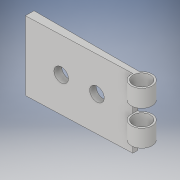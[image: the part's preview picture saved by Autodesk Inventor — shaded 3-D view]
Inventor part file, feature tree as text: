
AUTODESK INVENTOR PART (.ipt)
format: ipt  version: 2018 (Build 220112000, 112)  size: 144,896 bytes
history: native  units: in
note: dims shown in document units (in); Inventor stores cm internally (conversion verified against a paired STEP export)
features: extrude x4, sketch x4, plane x1
ambient origin geometry x8: Origin, YZ Plane, XZ Plane, XY Plane, X Axis, Y Axis, Z Axis, Center Point
bodies: Solid1 (feature_tree)
feature tree (9):
  extrude  "Extrusion1"  Depth=1.0in
  extrude  "Extrusion2"  Depth=0.5in
  plane  "Work Plane1"
  extrude  "Extrusion3"  Depth=0.2031in
  extrude  "Extrusion4"  Depth=0.25in
  sketch  "Sketch1"  dims[d0=1.5in d1=1.0in]
  sketch  "Sketch2"  dims[d2=0.5in d3=0.5in]
  sketch  "Sketch3"  dims[d4=0.2031in d5=0.2031in]
  sketch  "Sketch4"  dims[d6=0.125in d7=0.0in d8=0.25in d9=0.3in d10=0.25in d11=0.0in d12=0.25in d13=0.25in d14=0.0in d15=2.0in d16=0.0in]
